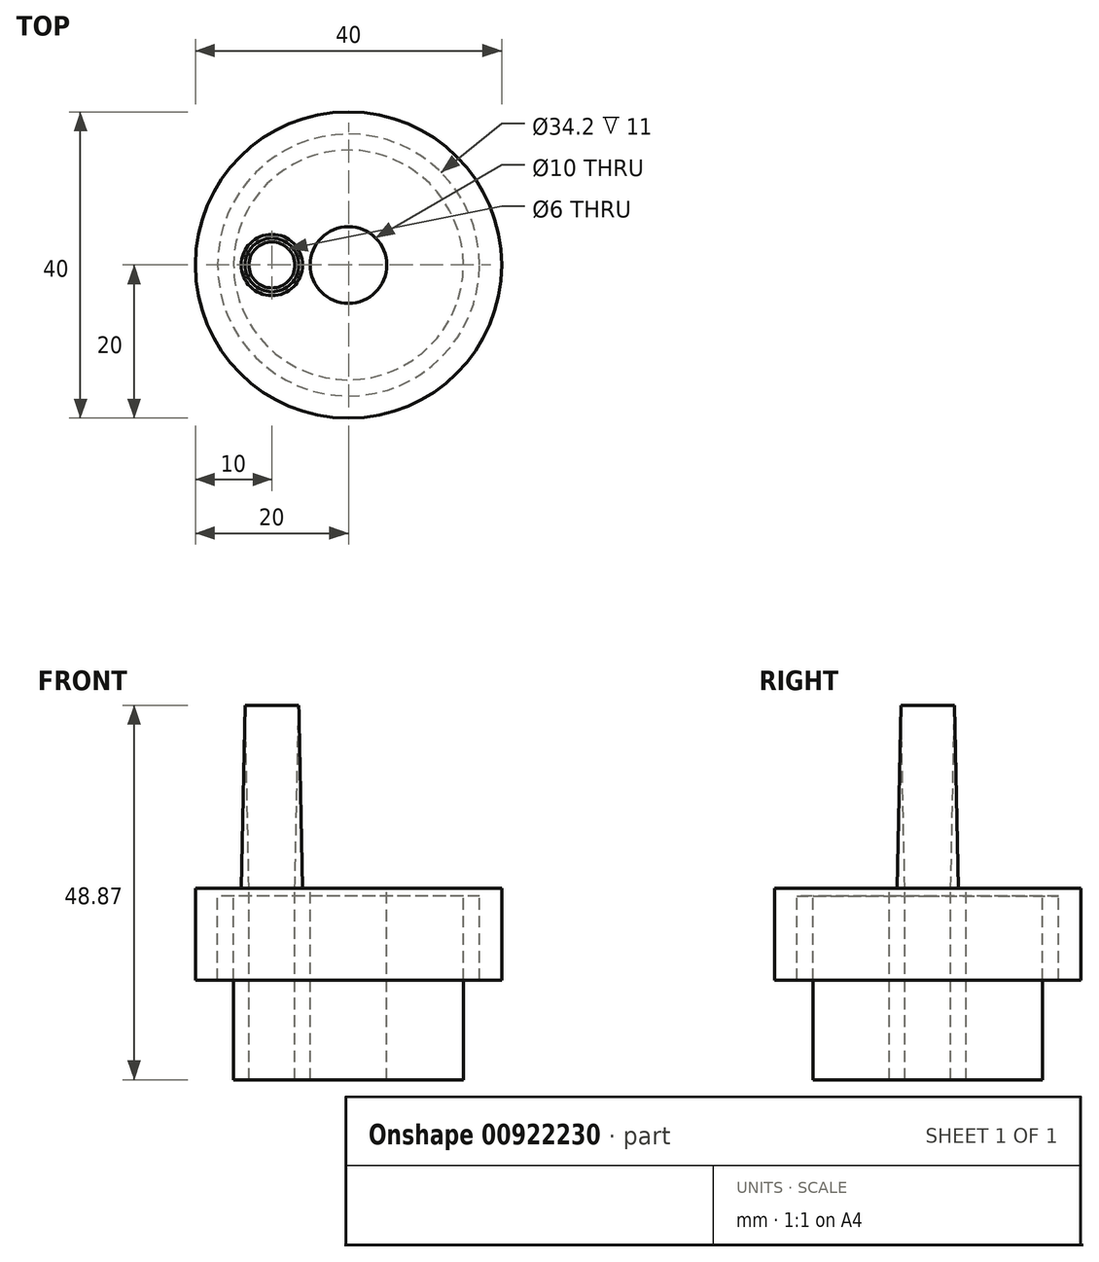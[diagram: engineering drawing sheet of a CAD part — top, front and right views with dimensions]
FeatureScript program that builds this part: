
annotation { "Feature Type Name" : "Feature", "Feature Type Description" : "" }
export const myFeature = defineFeature(function(context is Context, id is Id, definition is map)
    precondition{}
    {
        {
            var Q0;
            Q0=qCreatedBy(makeId("Front.planeOp"),FACE);
            var sketch = newSketch(context, id + "F0", { "sketchPlane" : qUnion([Q0])});
            skLineSegment(sketch, "E0", {"start": v(0, 0) * mm, "end": v(20, 0) * mm});
            skLineSegment(sketch, "E1", {"start": v(20, 0) * mm, "end": v(20, -12) * mm});
            skLineSegment(sketch, "E2", {"start": v(20, -12) * mm, "end": v(17.1, -12) * mm});
            skLineSegment(sketch, "E3", {"start": v(17.1, -12) * mm, "end": v(17.1, -1) * mm});
            skLineSegment(sketch, "E4", {"start": v(17.1, -1) * mm, "end": v(15, -1) * mm});
            skLineSegment(sketch, "E5", {"start": v(15, -1) * mm, "end": v(15, -25) * mm});
            skLineSegment(sketch, "E6", {"start": v(15, -25) * mm, "end": v(0, -25) * mm});
            skLineSegment(sketch, "E7", {"start": v(0, -25) * mm, "end": v(0, 0) * mm});
            skLineSegment(sketch, "E8", {"start": v(0, 12.07) * mm, "end": v(0, -53.6) * mm, "construction": true});
            skSolve(sketch);
        }
        {
            var Q0;
            Q0=makeQuery(id+"F0.imprint","IMPRINT",FACE,{"disambiguationData":[TD([[makeQuery(id+"F0.imprint","IMPRINT",EDGE,{"derivedFrom":sQuery(id+"F0.wireOp",EDGE,"E0")}),-1.0]])]});
            var Q1;
            Q1=sQuery(id+"F0.wireOp",EDGE,"E8");
            revolve(context, id + "F1", {"entities" : qUnion([Q0]), "axis" : qUnion([Q1]), "revolveType" : RevolveType.FULL});
        }
        {
            var Q0;
            Q0=qCreatedBy(makeId("Top.planeOp"),FACE);
            var sketch = newSketch(context, id + "F2", { "sketchPlane" : qUnion([Q0])});
            skCircle(sketch, "E9", {"center": v(0, 0) * mm, "radius": 5 * mm});
            skSolve(sketch);
        }
        {
            var Q0;
            Q0=qSketchRegion(id+"F2",true);
            extrude(context, id + "F3", {"entities" : qUnion([Q0]), "operationType" : NewBodyOperationType.REMOVE, "endBound" : BoundingType.THROUGH_ALL, "oppositeDirection" : true, "depth" : 25 * mm, "offsetDistance" : 25 * mm});
        }
        {
            var Q0;
            Q0=makeQuery(id+"F1.opRevolve","SWEPT_FACE",FACE,{"disambiguationData":[OSD([sQuery(id+"F0.wireOp",EDGE,"E0")])]});
            var sketch = newSketch(context, id + "F4", { "sketchPlane" : qUnion([Q0])});
            skCircle(sketch, "E10", {"center": v(-10, 0) * mm, "radius": 3 * mm});
            skSolve(sketch);
        }
        {
            var Q0;
            Q0=makeQuery(id+"F4.imprint","IMPRINT",FACE,{"disambiguationData":[TD([[makeQuery(id+"F4.imprint","IMPRINT",EDGE,{"derivedFrom":sQuery(id+"F4.wireOp",EDGE,"E10")}),1.0]])]});
            extrude(context, id + "F5", {"entities" : qUnion([Q0]), "operationType" : NewBodyOperationType.REMOVE, "endBound" : BoundingType.THROUGH_ALL, "oppositeDirection" : true, "depth" : 25 * mm, "offsetDistance" : 25 * mm});
        }
        {
            var Q0;
            Q0=makeQuery(id+"F1.opRevolve","SWEPT_FACE",FACE,{"disambiguationData":[OSD([sQuery(id+"F0.wireOp",EDGE,"E0")])]});
            var sketch = newSketch(context, id + "F6", { "sketchPlane" : qUnion([Q0])});
            skCircle(sketch, "E11", {"center": v(-10, 0) * mm, "radius": 3 * mm});
            skCircle(sketch, "E12", {"center": v(-10, 0) * mm, "radius": 4 * mm});
            skSolve(sketch);
        }
        {
            var Q0;
            Q0=makeQuery(id+"F6.imprint","IMPRINT",FACE,{"disambiguationData":[TD([[makeQuery(id+"F6.imprint","IMPRINT",EDGE,{"derivedFrom":sQuery(id+"F6.wireOp",EDGE,"E11")}),-1.0]])]});
            extrude(context, id + "F7", {"entities" : qUnion([Q0]), "operationType" : NewBodyOperationType.ADD, "depth" : 25 * mm, "offsetDistance" : 25 * mm, "hasDraft" : true, "draftAngle" : 1.2 * degree, "draftPullDirection" : true});
        }
    });
